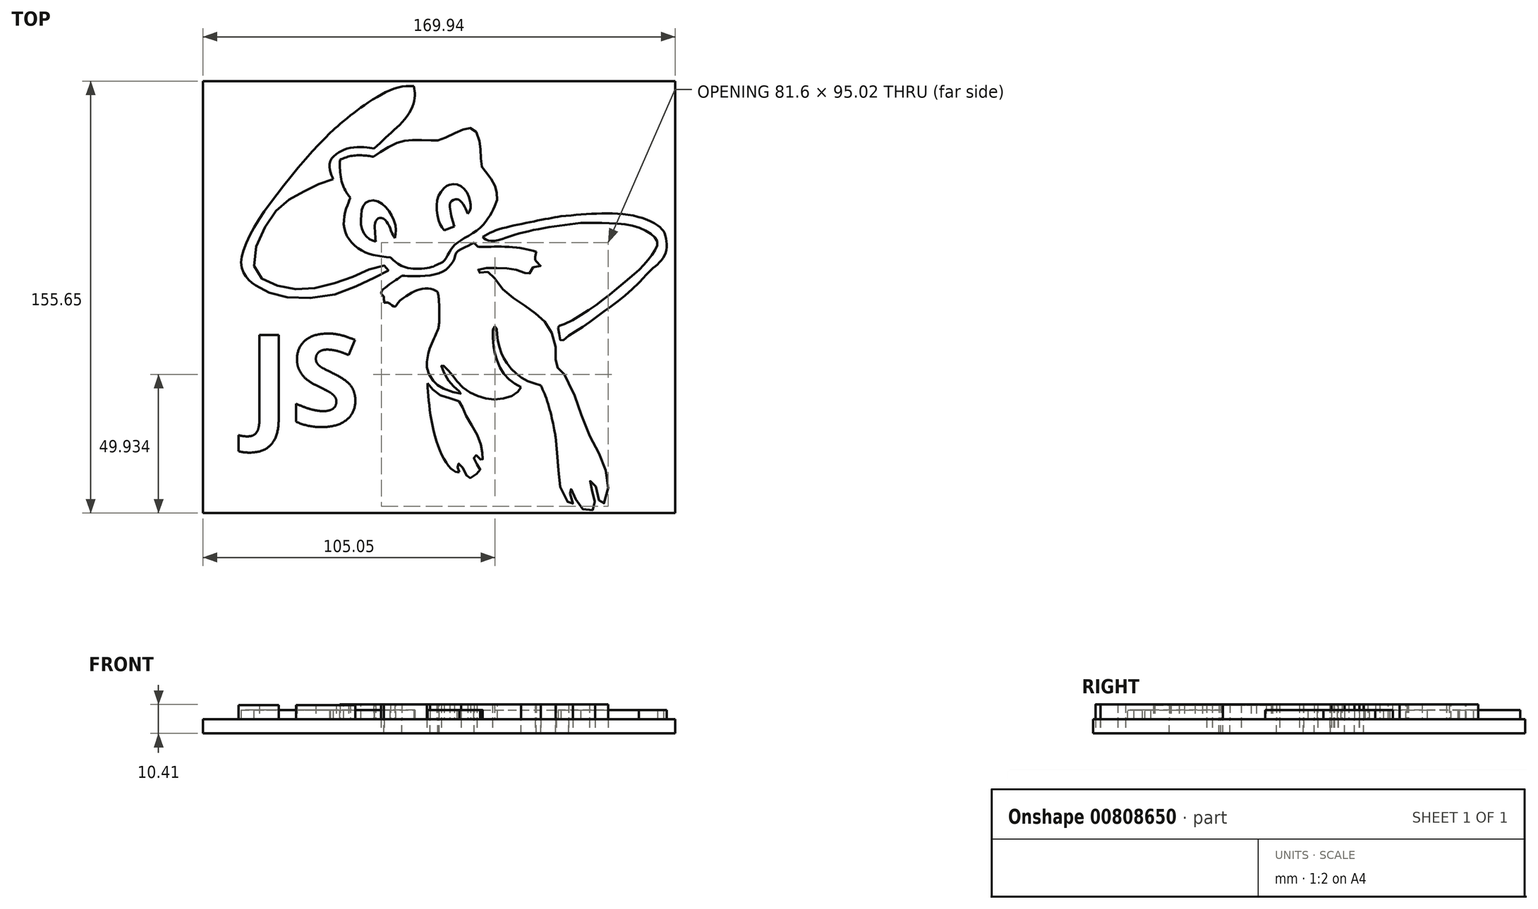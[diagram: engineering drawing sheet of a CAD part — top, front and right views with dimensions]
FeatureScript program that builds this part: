
annotation { "Feature Type Name" : "Feature", "Feature Type Description" : "" }
export const myFeature = defineFeature(function(context is Context, id is Id, definition is map)
    precondition{}
    {
        {
            var Q0;
            Q0=qCreatedBy(makeId("Top.planeOp"),FACE);
            var sketch = newSketch(context, id + "F0", { "sketchPlane" : qUnion([Q0])});
            skFitSpline(sketch, "E0", {"points": [v(-36.88, 36.08) * mm, v(-38.4, 38.25) * mm, v(-40.15, 42.6) * mm, v(-40.65, 48.33) * mm, v(-40.58, 49.85) * mm], "startDerivative": vector(-6.94, 9.09) * mm, "endDerivative": vector(0.6, 7.48) * mm});
            skFitSpline(sketch, "E1", {"points": [v(-40.58, 49.85) * mm, v(-38.04, 50.8) * mm, v(-34.93, 51.37) * mm, v(-31.38, 51.3) * mm, v(-28.55, 50.87) * mm], "startDerivative": vector(10.5, 4.31) * mm, "endDerivative": vector(11.28, -2.04) * mm});
            skFitSpline(sketch, "E2", {"points": [v(-28.55, 50.87) * mm, v(-24.87, 53.3) * mm, v(-19.99, 55.88) * mm, v(-16.36, 56.8) * mm, v(-12.2, 56.87) * mm, v(-6.98, 56.74) * mm, v(-4.41, 57) * mm, v(1, 59.57) * mm, v(4.83, 61.1) * mm, v(7.67, 60.76) * mm, v(9.65, 56.27) * mm, v(10.11, 52.11) * mm, v(10.44, 47.3) * mm, v(11.57, 45.71) * mm, v(14.54, 41.82) * mm, v(15.6, 38.91) * mm, v(16.05, 35.8) * mm, v(15.13, 32.97) * mm], "startDerivative": vector(55.8, 38.5) * mm, "endDerivative": vector(-24.9, -54.1) * mm});
            skFitSpline(sketch, "E3", {"points": [v(15.13, 32.97) * mm, v(13.23, 29.5) * mm, v(9.9, 25.32) * mm, v(3.54, 21.13) * mm, v(0, 18.38) * mm, v(-1.7, 15.62) * mm, v(-3.4, 13.15) * mm, v(-5.2, 12.2) * mm], "startDerivative": vector(-12.69, -24.26) * mm, "endDerivative": vector(-18.67, -6.95) * mm});
            skFitSpline(sketch, "E4", {"points": [v(-5.2, 12.2) * mm, v(-8.38, 10.92) * mm, v(-15.27, 10.68) * mm, v(-19.62, 12.2) * mm, v(-22.36, 14.64) * mm], "startDerivative": vector(-12.64, -6.7) * mm, "endDerivative": vector(-11.41, 11.76) * mm});
            skFitSpline(sketch, "E5", {"points": [v(-22.36, 14.64) * mm, v(-29.1, 15.62) * mm, v(-34.66, 18.38) * mm, v(-38.53, 23.3) * mm, v(-39.1, 28.91) * mm, v(-37.75, 33.9) * mm, v(-36.88, 36.08) * mm], "startDerivative": vector(-36.55, 3.17) * mm, "endDerivative": vector(7.3, 17.53) * mm});
            skFitSpline(sketch, "E6", {"points": [v(-27.74, 20.26) * mm, v(-28, 23.55) * mm, v(-27.97, 26.8) * mm, v(-27.14, 28.47) * mm, v(-25.9, 28.88) * mm, v(-24.15, 27.82) * mm, v(-22.83, 25.7) * mm, v(-21.65, 22.95) * mm, v(-20.94, 21.55) * mm], "startDerivative": vector(-1.85, 21.58) * mm, "endDerivative": vector(6.7, -12.08) * mm});
            skFitSpline(sketch, "E7", {"points": [v(-20.94, 21.55) * mm, v(-20.44, 24.42) * mm, v(-21.43, 28.58) * mm, v(-23.73, 32.29) * mm, v(-27.18, 34.9) * mm, v(-30.4, 34.9) * mm, v(-32.4, 32.97) * mm, v(-32.96, 29.53) * mm, v(-32.93, 25.74) * mm, v(-31.6, 22.72) * mm, v(-29.48, 20.98) * mm, v(-27.74, 20.26) * mm], "startDerivative": vector(8.86, 31.93) * mm, "endDerivative": vector(24.92, -8.61) * mm});
            skLineSegment(sketch, "E8", {"start": v(0.64, 25.77) * mm, "end": v(-3.1, 24.33) * mm});
            skFitSpline(sketch, "E9", {"points": [v(-3.1, 24.33) * mm, v(-4.7, 26.86) * mm, v(-5.73, 31.34) * mm, v(-5.33, 36.17) * mm, v(-3.1, 39.67) * mm, v(-0.97, 40.88) * mm, v(1.96, 40.82) * mm, v(4.95, 38.23) * mm, v(6.27, 34.79) * mm, v(6.39, 32.09) * mm, v(5.4, 30.37) * mm], "startDerivative": vector(-18.53, 24.2) * mm, "endDerivative": vector(-15.72, -20.8) * mm});
            skFitSpline(sketch, "E10", {"points": [v(5.4, 30.37) * mm, v(4.03, 33.3) * mm, v(2.36, 35.3) * mm, v(1.16, 35.6) * mm, v(-0.68, 34.67) * mm, v(-1.02, 32.66) * mm, v(-0.68, 30.37) * mm, v(0, 27.55) * mm, v(0.64, 25.77) * mm], "startDerivative": vector(-8.23, 19.96) * mm, "endDerivative": vector(5.68, -14.34) * mm});
            skFitSpline(sketch, "E11", {"points": [v(-28.3, 53.85) * mm, v(-22.62, 59.17) * mm, v(-17.41, 64.25) * mm, v(-14.15, 69.88) * mm, v(-13.66, 73.45) * mm, v(-13.97, 76.31) * mm], "startDerivative": vector(23.72, 22.62) * mm, "endDerivative": vector(-2.81, 19.35) * mm});
            skFitSpline(sketch, "E12", {"points": [v(-13.97, 76.31) * mm, v(-19.11, 76) * mm, v(-25.25, 73.58) * mm, v(-32.16, 69.26) * mm, v(-37.13, 65.53) * mm, v(-41.53, 61.88) * mm, v(-44.08, 59.5) * mm], "startDerivative": vector(-32.41, 0.3) * mm, "endDerivative": vector(-18.17, -17.44) * mm});
            skFitSpline(sketch, "E13", {"points": [v(-44.08, 59.5) * mm, v(-51.8, 51.48) * mm, v(-63.2, 37.48) * mm, v(-71.34, 25.77) * mm, v(-75.54, 16.64) * mm, v(-76.22, 11.77) * mm, v(-74.95, 8.38) * mm, v(-73.1, 6.15) * mm, v(-70.98, 4.61) * mm], "startDerivative": vector(-48.4, -47.85) * mm, "endDerivative": vector(29.7, -19.4) * mm});
            skFitSpline(sketch, "E14", {"points": [v(-70.98, 4.61) * mm, v(-65.73, 1.76) * mm, v(-56.11, 0) * mm, v(-41.53, 1.5) * mm, v(-30.47, 6.38) * mm, v(-23.8, 9.45) * mm, v(-22.65, 11) * mm, v(-25.86, 11.63) * mm, v(-32.16, 9.32) * mm, v(-40.09, 6.12) * mm, v(-50.09, 3.56) * mm, v(-58.94, 3.43) * mm, v(-66.88, 5.86) * mm, v(-70.98, 9.58) * mm, v(-70.98, 17.91) * mm, v(-66.24, 27.79) * mm, v(-60.86, 34.07) * mm, v(-54.7, 37.79) * mm, v(-48.55, 40.86) * mm, v(-43.04, 42.79) * mm], "startDerivative": vector(103.96, -66.84) * mm, "endDerivative": vector(119.1, 36.89) * mm});
            skFitSpline(sketch, "E15", {"points": [v(-43.04, 42.79) * mm, v(-44.08, 45.32) * mm, v(-44.08, 49.34) * mm, v(-41, 52.5) * mm, v(-36.55, 54.15) * mm, v(-31.3, 54.3) * mm, v(-28.3, 53.85) * mm], "startDerivative": vector(-8.33, 16.7) * mm, "endDerivative": vector(18.9, -3.53) * mm});
            skFitSpline(sketch, "E16", {"points": [v(7.73, 19.96) * mm, v(4.7, 18.38) * mm, v(1.47, 16.59) * mm, v(0.64, 14.22) * mm, v(-1.21, 11.37) * mm, v(-4.34, 9.18) * mm, v(-10.33, 7.93) * mm, v(-15.9, 7.9) * mm, v(-18.3, 8) * mm], "startDerivative": vector(-23.75, -13.65) * mm, "endDerivative": vector(-21.58, 1.02) * mm});
            skFitSpline(sketch, "E17", {"points": [v(-18.3, 8) * mm, v(-21.48, 5.79) * mm, v(-25.73, 2.22) * mm, v(-25.51, 1.24) * mm, v(-24.96, 0.69) * mm, v(-24.75, -0.76) * mm, v(-24.75, -1.78) * mm], "startDerivative": vector(-11.77, -8.3) * mm, "endDerivative": vector(-0.07, -7.72) * mm});
            skFitSpline(sketch, "E18", {"points": [v(-24.75, -1.78) * mm, v(-23.18, -1.78) * mm, v(-20.94, -3.12) * mm, v(-19.7, -1.78) * mm, v(-15.31, 1.57) * mm, v(-11.82, 3.08) * mm, v(-8.28, 3.4) * mm, v(-5.41, 2.2) * mm], "startDerivative": vector(14.29, 3.8) * mm, "endDerivative": vector(18.83, -10.57) * mm});
            skFitSpline(sketch, "E19", {"points": [v(-5.41, -11.46) * mm, v(-6.46, -13.9) * mm, v(-8.5, -18.88) * mm, v(-9.27, -22.77) * mm, v(-9.19, -25.46) * mm, v(-8.23, -28.1) * mm], "startDerivative": vector(-5.21, -12.45) * mm, "endDerivative": vector(6.45, -14.59) * mm});
            skFitSpline(sketch, "E20", {"points": [v(-5.41, -11.46) * mm, v(-5.02, -10.14) * mm, v(-4.86, -5.9) * mm, v(-5.02, -0.37) * mm, v(-5.41, 2.2) * mm], "startDerivative": vector(2.76, 6.94) * mm, "endDerivative": vector(-2.02, 10.26) * mm});
            skFitSpline(sketch, "E21", {"points": [v(-8.23, -28.1) * mm, v(-6.3, -30.62) * mm, v(-2.7, -32.95) * mm, v(3.02, -34.4) * mm, v(1.33, -32.7) * mm, v(-2.6, -28.1) * mm, v(-3.98, -24.1) * mm, v(-2.53, -25.15) * mm, v(0, -28.1) * mm, v(3.82, -32.39) * mm, v(9.45, -35.44) * mm, v(15.89, -36.57) * mm, v(22.56, -34.56) * mm, v(24.65, -32.14) * mm], "startDerivative": vector(28.07, -40.83) * mm, "endDerivative": vector(24.08, 39.06) * mm});
            skFitSpline(sketch, "E22", {"points": [v(24.65, -32.14) * mm, v(19.46, -28.61) * mm, v(16.04, -22.68) * mm, v(14.52, -16.3) * mm, v(14.9, -10.44) * mm, v(15.66, -10.59) * mm, v(15.96, -13.48) * mm, v(17.1, -18.5) * mm, v(18.55, -22.07) * mm, v(21.74, -26.25) * mm, v(26.3, -29.6) * mm, v(31.7, -31.5) * mm], "startDerivative": vector(-53.5, 28.4) * mm, "endDerivative": vector(55.72, -15.9) * mm});
            skFitSpline(sketch, "E23", {"points": [v(31.7, -31.5) * mm, v(33.83, -36.52) * mm, v(35.88, -44.2) * mm, v(36.72, -48.3) * mm, v(37.03, -50.06) * mm], "startDerivative": vector(8, -16.8) * mm, "endDerivative": vector(1.73, -10.31) * mm});
            skFitSpline(sketch, "E24", {"points": [v(37.03, -50.06) * mm, v(37.67, -56.88) * mm, v(38.28, -65.1) * mm, v(40.12, -71.84) * mm, v(43.18, -74.9) * mm, v(43.1, -73.5) * mm, v(42.4, -70.97) * mm, v(41.78, -68.6) * mm, v(42.74, -69.04) * mm, v(44.05, -72.02) * mm, v(46.24, -75.6) * mm, v(48.43, -76.56) * mm, v(50.96, -76.04) * mm, v(51.14, -73.77) * mm, v(50.44, -70) * mm, v(49.3, -67.03) * mm, v(49.65, -65.8) * mm, v(50.96, -67.03) * mm, v(52.28, -70.88) * mm, v(53.41, -74.73) * mm, v(55.25, -72.45) * mm, v(55.69, -64.58) * mm, v(52.89, -56.53) * mm, v(48, -46.82) * mm, v(43.88, -35.1) * mm, v(41.78, -30.72) * mm], "startDerivative": vector(13.24, -128.19) * mm, "endDerivative": vector(-47.37, 85.69) * mm});
            skFitSpline(sketch, "E25", {"points": [v(41.78, -30.72) * mm, v(39.73, -27.08) * mm, v(37.25, -24.41) * mm, v(37.25, -19.83) * mm, v(34.98, -11.16) * mm, v(30.4, -6) * mm, v(23.99, -1.41) * mm, v(17.4, 3.84) * mm, v(13.4, 9.09) * mm, v(11.07, 9.25) * mm, v(8.74, 9.34) * mm, v(9.57, 10.42) * mm, v(12.82, 10.75) * mm, v(17.74, 10.75) * mm, v(21.82, 10.34) * mm, v(25.32, 9.42) * mm, v(27.49, 8.42) * mm, v(27.82, 9.75) * mm, v(29.73, 11.34) * mm, v(31.7, 11.67) * mm, v(30.07, 13.17) * mm], "startDerivative": vector(-32.27, 75.78) * mm, "endDerivative": vector(-69.54, 49.62) * mm});
            skFitSpline(sketch, "E26", {"points": [v(30.07, 13.17) * mm, v(29.68, 13.9) * mm, v(30.07, 16.7) * mm], "startDerivative": vector(-1.4, 1.7) * mm, "endDerivative": vector(1.15, 5.02) * mm});
            skFitSpline(sketch, "E27", {"points": [v(30.07, 16.7) * mm, v(22.73, 18.2) * mm, v(13.95, 18.48) * mm, v(10.79, 18.39) * mm, v(9.05, 18.57) * mm, v(7.73, 19.96) * mm], "startDerivative": vector(-25.6, 6.72) * mm, "endDerivative": vector(-8.87, 12.5) * mm});
            skFitSpline(sketch, "E28", {"points": [v(2.36, -62.8) * mm, v(0.76, -62.5) * mm, v(-2.57, -59) * mm, v(-6.3, -50.06) * mm, v(-8.47, -38.73) * mm, v(-9.1, -30.72) * mm], "startDerivative": vector(-15.3, 0.2) * mm, "endDerivative": vector(-2, 34.43) * mm});
            skFitSpline(sketch, "E29", {"points": [v(-9.1, -30.72) * mm, v(-6.83, -33.36) * mm, v(-2.86, -35.76) * mm, v(1.7, -36.87) * mm, v(3.27, -38.68) * mm, v(4.67, -42.12) * mm, v(7.73, -47.26) * mm, v(9.98, -52.26) * mm, v(10.68, -55.72) * mm, v(10.74, -57.77) * mm, v(10.68, -58.76) * mm, v(9.52, -57.7) * mm, v(8.4, -56.66) * mm, v(7.73, -56.9) * mm, v(7.73, -58) * mm, v(9, -60.22) * mm, v(9.87, -61.8) * mm, v(9.4, -62.79) * mm, v(7, -64.42) * mm, v(5.66, -64.95) * mm, v(4.55, -62.96) * mm, v(3.15, -60.4) * mm, v(2.1, -59.64) * mm, v(1.63, -60.1) * mm, v(1.87, -61.39) * mm, v(2.36, -62.8) * mm], "startDerivative": vector(41.4, -54) * mm, "endDerivative": vector(14.87, -42.66) * mm});
            skFitSpline(sketch, "E30", {"points": [v(10.72, 22.02) * mm, v(15.3, 24.28) * mm, v(23.56, 26.44) * mm, v(32.84, 28.33) * mm, v(38.94, 29.4) * mm], "startDerivative": vector(20, 11.39) * mm, "endDerivative": vector(24.9, 4.23) * mm});
            skFitSpline(sketch, "E31", {"points": [v(10.72, 22.02) * mm, v(12.02, 21) * mm, v(14.93, 20.56) * mm, v(20, 22.02) * mm, v(27.23, 24.07) * mm, v(36.57, 25.8) * mm, v(46, 27.03) * mm], "startDerivative": vector(12.39, -12.48) * mm, "endDerivative": vector(43.26, 5.28) * mm});
            skFitSpline(sketch, "E32", {"points": [v(46, 27.03) * mm, v(54.46, 27.03) * mm, v(64.58, 26.06) * mm, v(71.34, 23.07) * mm, v(73.7, 20) * mm, v(72.38, 16.45) * mm, v(68.06, 11.1) * mm, v(62.98, 6.64) * mm, v(59.01, 3.36) * mm], "startDerivative": vector(56.72, 0.57) * mm, "endDerivative": vector(-34.14, -28.32) * mm});
            skFitSpline(sketch, "E33", {"points": [v(38.94, 29.4) * mm, v(48.57, 30.24) * mm, v(58.73, 30.38) * mm, v(68.13, 28.85) * mm, v(73.84, 26.06) * mm, v(75.93, 24.11) * mm], "startDerivative": vector(41.77, 4.1) * mm, "endDerivative": vector(14.3, -15.48) * mm});
            skFitSpline(sketch, "E34", {"points": [v(59.01, 3.36) * mm, v(52.8, -1.66) * mm, v(46, -6.28) * mm, v(38.94, -9.92) * mm, v(37.93, -10.28) * mm, v(38.17, -12.05) * mm, v(38.94, -15.45) * mm, v(41.63, -13.75) * mm, v(47.58, -9.92) * mm, v(54.08, -5.19) * mm, v(60.39, -0.45) * mm, v(67.07, 5.5) * mm], "startDerivative": vector(-56.72, -47.28) * mm, "endDerivative": vector(57.6, 53.68) * mm});
            skFitSpline(sketch, "E35", {"points": [v(67.07, 5.5) * mm, v(71.5, 10.15) * mm, v(76.76, 16.45) * mm, v(75.93, 24.11) * mm], "startDerivative": vector(12.97, 14.55) * mm, "endDerivative": vector(-7.34, 15.71) * mm});
            skSolve(sketch);
        }
        {
            var Q0;
            Q0=makeQuery(id+"F0.imprint","IMPRINT",FACE,{"disambiguationData":[TD([[makeQuery(id+"F0.imprint","IMPRINT",EDGE,{"derivedFrom":sQuery(id+"F0.wireOp",EDGE,"E0")}),-1.0]])]});
            var Q1;
            Q1=makeQuery(id+"F0.imprint","IMPRINT",FACE,{"disambiguationData":[TD([[makeQuery(id+"F0.imprint","IMPRINT",EDGE,{"derivedFrom":sQuery(id+"F0.wireOp",EDGE,"E16")}),1.0]])]});
            extrude(context, id + "F1", {"entities" : qUnion([Q0, Q1]), "depth" : 5.33 * mm});
        }
        {
            var Q0;
            Q0=makeQuery(id+"F0.imprint","IMPRINT",FACE,{"disambiguationData":[TD([[makeQuery(id+"F0.imprint","IMPRINT",EDGE,{"derivedFrom":sQuery(id+"F0.wireOp",EDGE,"E11")}),1.0]])]});
            var Q1;
            Q1=makeQuery(id+"F0.imprint","IMPRINT",FACE,{"disambiguationData":[TD([[makeQuery(id+"F0.imprint","IMPRINT",EDGE,{"derivedFrom":sQuery(id+"F0.wireOp",EDGE,"E28")}),-1.0]])]});
            var Q2;
            Q2=makeQuery(id+"F0.imprint","IMPRINT",FACE,{"disambiguationData":[TD([[makeQuery(id+"F0.imprint","IMPRINT",EDGE,{"derivedFrom":sQuery(id+"F0.wireOp",EDGE,"E30")}),-1.0]])]});
            extrude(context, id + "F2", {"entities" : qUnion([Q0, Q1, Q2]), "depth" : 3.3 * mm});
        }
        {
            var Q0;
            Q0=makeQuery(id+"F1.opExtrude","CAP_FACE",FACE,{"disambiguationData":[OSD([sQuery(id+"F0.wireOp",EDGE,"E16"),sQuery(id+"F0.wireOp",EDGE,"E17"),sQuery(id+"F0.wireOp",EDGE,"E18"),sQuery(id+"F0.wireOp",EDGE,"E19"),sQuery(id+"F0.wireOp",EDGE,"E20"),sQuery(id+"F0.wireOp",EDGE,"E21"),sQuery(id+"F0.wireOp",EDGE,"E22"),sQuery(id+"F0.wireOp",EDGE,"E23"),sQuery(id+"F0.wireOp",EDGE,"E24"),sQuery(id+"F0.wireOp",EDGE,"E25"),sQuery(id+"F0.wireOp",EDGE,"E26"),sQuery(id+"F0.wireOp",EDGE,"E27")])],"isStart":true});
            var sketch = newSketch(context, id + "F3", { "sketchPlane" : qUnion([Q0])});
            skLineSegment(sketch, "E36.bottom", {"start": v(80.03, 77.48) * mm, "end": v(-89.91, 77.48) * mm});
            skLineSegment(sketch, "E36.top", {"start": v(80.03, -78.17) * mm, "end": v(-89.91, -78.17) * mm});
            skLineSegment(sketch, "E36.left", {"start": v(80.03, 77.48) * mm, "end": v(80.03, -78.17) * mm});
            skLineSegment(sketch, "E36.right", {"start": v(-89.91, 77.48) * mm, "end": v(-89.91, -78.17) * mm});
            skSolve(sketch);
        }
        {
            var Q0;
            Q0=makeQuery(id+"F3.imprint","IMPRINT",FACE,{"disambiguationData":[TD([[makeQuery(id+"F3.imprint","IMPRINT",EDGE,{"derivedFrom":sQuery(id+"F3.wireOp",EDGE,"E36.bottom")}),1.0]])]});
            extrude(context, id + "F4", {"entities" : qUnion([Q0]), "depth" : 5.08 * mm, "offsetDistance" : 25.4 * mm});
        }
        {
            var Q0;
            Q0=makeQuery(id+"F1.opExtrude","CAP_FACE",FACE,{"disambiguationData":[OSD([sQuery(id+"F0.wireOp",EDGE,"E16"),sQuery(id+"F0.wireOp",EDGE,"E17"),sQuery(id+"F0.wireOp",EDGE,"E18"),sQuery(id+"F0.wireOp",EDGE,"E19"),sQuery(id+"F0.wireOp",EDGE,"E20"),sQuery(id+"F0.wireOp",EDGE,"E21"),sQuery(id+"F0.wireOp",EDGE,"E22"),sQuery(id+"F0.wireOp",EDGE,"E23"),sQuery(id+"F0.wireOp",EDGE,"E24"),sQuery(id+"F0.wireOp",EDGE,"E25"),sQuery(id+"F0.wireOp",EDGE,"E26"),sQuery(id+"F0.wireOp",EDGE,"E27")])],"isStart":true});
            extrude(context, id + "F5", {"entities" : qUnion([Q0]), "depth" : 5.08 * mm, "offsetDistance" : 25.4 * mm});
        }
        {
            var Q0;
            Q0=makeQuery(id+"F4.opExtrude","CAP_FACE",FACE,{"disambiguationData":[OSD([sQuery(id+"F0.wireOp",EDGE,"E16"),sQuery(id+"F0.wireOp",EDGE,"E17"),sQuery(id+"F0.wireOp",EDGE,"E18"),sQuery(id+"F0.wireOp",EDGE,"E19"),sQuery(id+"F0.wireOp",EDGE,"E20"),sQuery(id+"F0.wireOp",EDGE,"E21"),sQuery(id+"F0.wireOp",EDGE,"E22"),sQuery(id+"F0.wireOp",EDGE,"E23"),sQuery(id+"F0.wireOp",EDGE,"E24"),sQuery(id+"F0.wireOp",EDGE,"E25"),sQuery(id+"F0.wireOp",EDGE,"E26"),sQuery(id+"F0.wireOp",EDGE,"E27"),sQuery(id+"F3.wireOp",EDGE,"E36.bottom"),sQuery(id+"F3.wireOp",EDGE,"E36.top"),sQuery(id+"F3.wireOp",EDGE,"E36.left"),sQuery(id+"F3.wireOp",EDGE,"E36.right")])],"isStart":true});
            var sketch = newSketch(context, id + "F6", { "sketchPlane" : qUnion([Q0])});
            skText(sketch, "E37", { "text": "JS", "fontName": "OpenSans-Bold.ttf"});
            const initialGuessF6  = {"E37": [-0.07378, -0.04606, 1, 0, 0.03306]};
            skSetInitialGuess(sketch, initialGuessF6);
            skSolve(sketch);
        }
        {
            var Q0;
            Q0=qSketchRegion(id+"F6",true);
            extrude(context, id + "F7", {"entities" : qUnion([Q0]), "operationType" : NewBodyOperationType.ADD, "depth" : 5.08 * mm, "offsetDistance" : 25.4 * mm});
        }
    });
